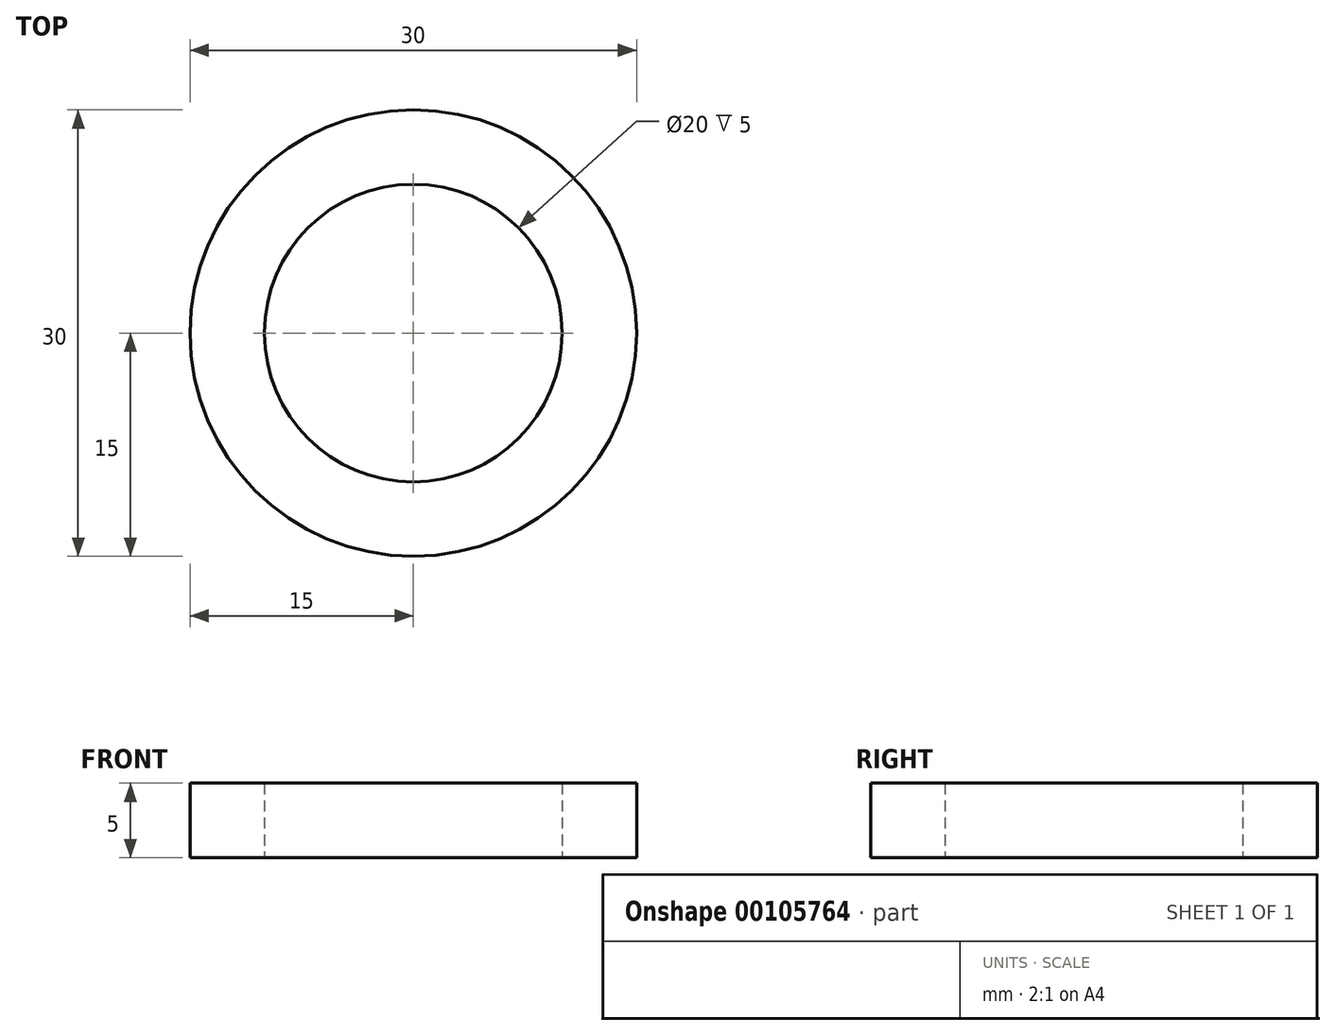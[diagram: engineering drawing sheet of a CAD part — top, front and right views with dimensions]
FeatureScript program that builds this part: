
annotation { "Feature Type Name" : "Feature", "Feature Type Description" : "" }
export const myFeature = defineFeature(function(context is Context, id is Id, definition is map)
    precondition{}
    {
        {
            var Q0;
            Q0=qCreatedBy(makeId("Top.planeOp"),FACE);
            var sketch = newSketch(context, id + "F0", { "sketchPlane" : qUnion([Q0])});
            skCircle(sketch, "E0", {"center": v(0, 0) * mm, "radius": 10 * mm});
            skCircle(sketch, "E1", {"center": v(0, 0) * mm, "radius": 15 * mm});
            skSolve(sketch);
        }
        {
            var Q0;
            Q0=makeQuery(id+"F0.imprint","IMPRINT",FACE,{"disambiguationData":[TD([[makeQuery(id+"F0.imprint","IMPRINT",EDGE,{"derivedFrom":sQuery(id+"F0.wireOp",EDGE,"E0")}),-1.0]])]});
            extrude(context, id + "F1", {"entities" : qUnion([Q0]), "depth" : 5 * mm});
        }
    });
